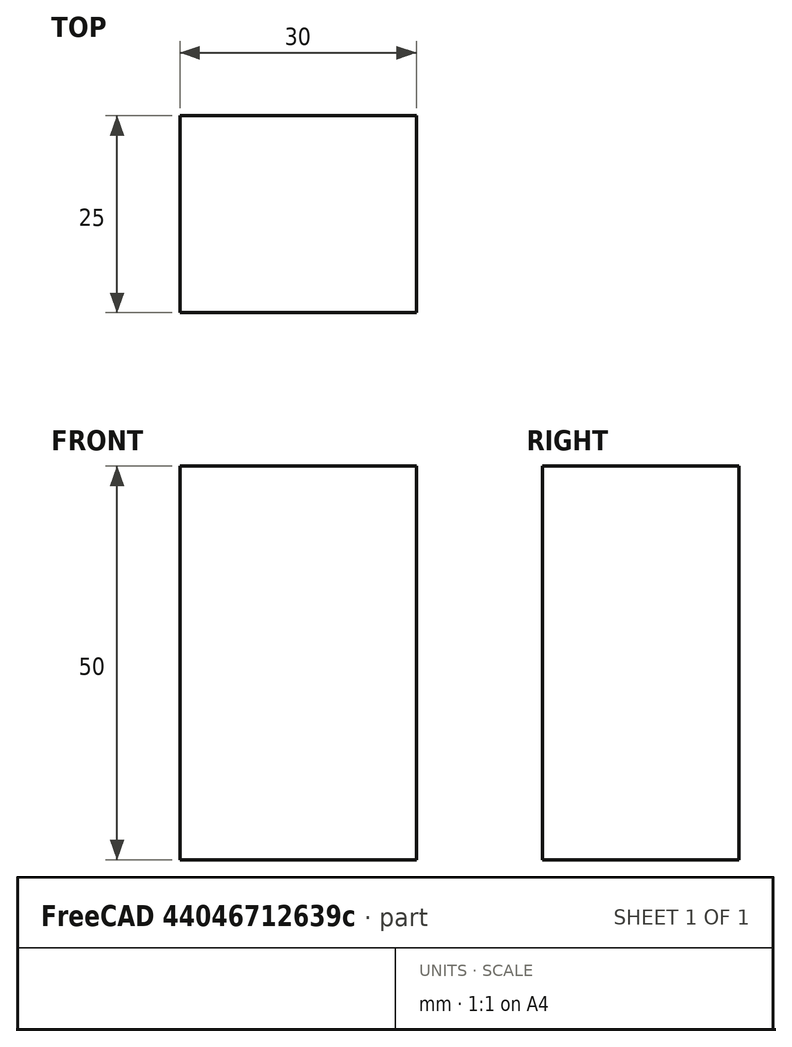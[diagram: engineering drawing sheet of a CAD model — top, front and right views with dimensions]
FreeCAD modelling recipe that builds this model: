
FCSTD DOCUMENT  (FreeCAD 0.15R4671 (Git))
Label: Flat Bar 30x25 EN10058 S235JR
License: All rights reserved
LicenseURL: http://en.wikipedia.org/wiki/All_rights_reserved
objects: Sketcher::SketchObject×1, Part::Extrusion×1
note: 2 computed .brp shape members not serialized (recipe doc carries the construction recipe); baked Part::Feature solids carry a one-line shape summary decoded from their .brp

FEATURE [Sketcher::SketchObject] Sketch
  sketch-geometry (4):
    g0: LineSegment StartX=-15 StartY=-12.5 StartZ=0 EndX=15 EndY=-12.5 EndZ=0
    g1: LineSegment StartX=15 StartY=-12.5 StartZ=0 EndX=15 EndY=12.5 EndZ=0
    g2: LineSegment StartX=15 StartY=12.5 StartZ=0 EndX=-15 EndY=12.5 EndZ=0
    g3: LineSegment StartX=-15 StartY=12.5 StartZ=0 EndX=-15 EndY=-12.5 EndZ=0
  constraints (12):
    c: Coincident(g0,g1)
    c: Coincident(g1,g2)
    c: Coincident(g2,g3)
    c: Coincident(g3,g0)
    c: Horizontal(g0)
    c: Horizontal(g2)
    c: Vertical(g1)
    c: Vertical(g3)
    c: Symmetric(g1,g2,g-2)
    c: Symmetric(g0,g1,g-1)
    c: DistanceY(g1) = 25
    c: DistanceX(g0) = 30
FEATURE [Part::Extrusion] Extrude  label="Flat Bar 30x25 EN10058 S235JR"
  Base = -> Sketch
  Dir = (0,0,50)
  Solid = true
